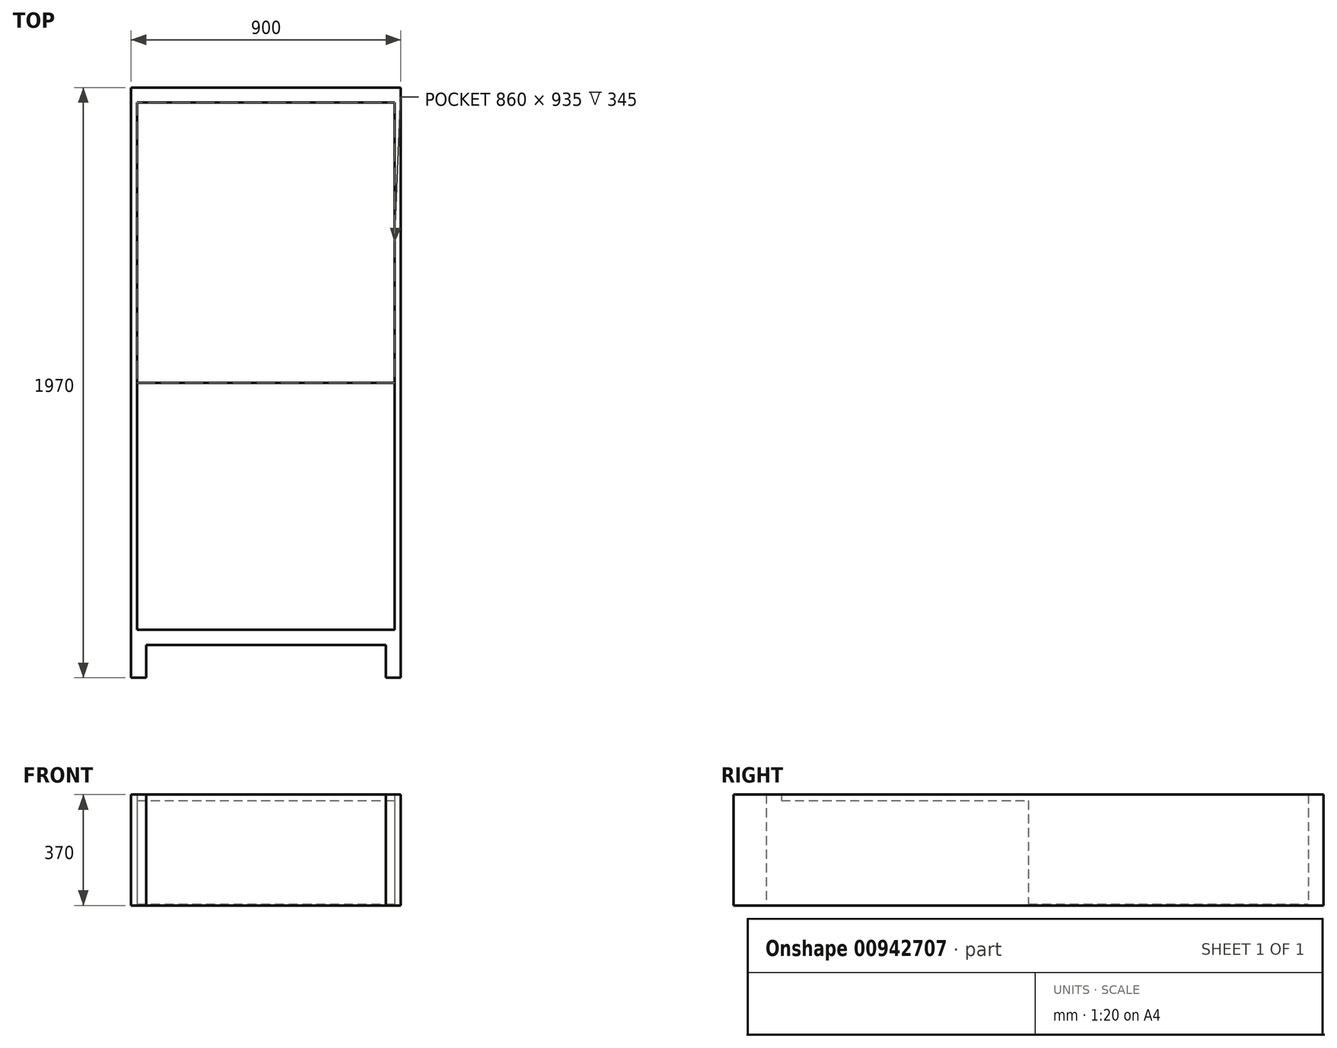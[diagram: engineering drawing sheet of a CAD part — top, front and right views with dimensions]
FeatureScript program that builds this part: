
annotation { "Feature Type Name" : "Feature", "Feature Type Description" : "" }
export const myFeature = defineFeature(function(context is Context, id is Id, definition is map)
    precondition{}
    {
        {
            var Q0;
            Q0=qCreatedBy(makeId("Top.planeOp"),FACE);
            var sketch = newSketch(context, id + "F0", { "sketchPlane" : qUnion([Q0])});
            skLineSegment(sketch, "E0.bottom", {"start": v(-450, 985) * mm, "end": v(450, 985) * mm});
            skLineSegment(sketch, "E0.left", {"start": v(-450, 985) * mm, "end": v(-450, -985) * mm});
            skLineSegment(sketch, "E0.right", {"start": v(450, 985) * mm, "end": v(450, -985) * mm});
            skLineSegment(sketch, "E1", {"start": v(-450, 0) * mm, "end": v(0, 0) * mm, "construction": true});
            skLineSegment(sketch, "E2", {"start": v(0, 0) * mm, "end": v(450, 0) * mm, "construction": true});
            skLineSegment(sketch, "E3", {"start": v(0, -985) * mm, "end": v(0, 0) * mm, "construction": true});
            skLineSegment(sketch, "E4", {"start": v(0, 0) * mm, "end": v(0, 985) * mm, "construction": true});
            skLineSegment(sketch, "E5", {"start": v(-400, -985) * mm, "end": v(-400, -875) * mm});
            skLineSegment(sketch, "E6", {"start": v(-400, -875) * mm, "end": v(400, -875) * mm});
            skLineSegment(sketch, "E7", {"start": v(400, -875) * mm, "end": v(400, -985) * mm});
            skLineSegment(sketch, "E8.trimOffspring", {"start": v(400, -985) * mm, "end": v(450, -985) * mm});
            skLineSegment(sketch, "E9", {"start": v(-400, -985) * mm, "end": v(-450, -985) * mm});
            skLineSegment(sketch, "E10.bottom", {"start": v(-430, -825) * mm, "end": v(430, -825) * mm});
            skLineSegment(sketch, "E10.top", {"start": v(-430, 935) * mm, "end": v(430, 935) * mm});
            skLineSegment(sketch, "E10.left", {"start": v(-430, -825) * mm, "end": v(-430, 935) * mm});
            skLineSegment(sketch, "E10.right", {"start": v(430, -825) * mm, "end": v(430, 935) * mm});
            skLineSegment(sketch, "E11", {"start": v(-430, 0) * mm, "end": v(430, 0) * mm});
            skSolve(sketch);
        }
        {
            var Q0;
            Q0=makeQuery(id+"F0.imprint","IMPRINT",FACE,{"disambiguationData":[TD([[makeQuery(id+"F0.imprint","IMPRINT",EDGE,{"derivedFrom":sQuery(id+"F0.wireOp",EDGE,"E0.bottom")}),-1.0]])]});
            extrude(context, id + "F1", {"entities" : qUnion([Q0]), "depth" : 370 * mm, "offsetDistance" : 25 * mm});
        }
        {
            var Q0;
            Q0=makeQuery(id+"F0.imprint","IMPRINT",FACE,{"disambiguationData":[TD([[makeQuery(id+"F0.imprint","IMPRINT",EDGE,{"derivedFrom":sQuery(id+"F0.wireOp",EDGE,"E10.bottom")}),1.0]])]});
            var Q1;
            {var subQ0=sQuery(id+"F0.wireOp",EDGE,"E10.top");Q1=makeQuery(id+"F0.imprint","IMPRINT",FACE,{"disambiguationData":[TD([[makeQuery(id+"F0.imprint","IMPRINT",EDGE,{"derivedFrom":subQ0}),-1.0]])]});}
            extrude(context, id + "F2", {"entities" : qUnion([Q0, Q1]), "operationType" : NewBodyOperationType.ADD, "depth" : 5 * mm, "offsetDistance" : 25 * mm});
        }
        {
            var Q0;
            Q0=makeQuery(id+"F1.opExtrude","SWEPT_BODY",BODY,{"disambiguationData":[OSD([sQuery(id+"F0.wireOp",EDGE,"E0.bottom"),sQuery(id+"F0.wireOp",EDGE,"E0.left"),sQuery(id+"F0.wireOp",EDGE,"E0.right"),sQuery(id+"F0.wireOp",EDGE,"E5"),sQuery(id+"F0.wireOp",EDGE,"E6"),sQuery(id+"F0.wireOp",EDGE,"E7"),sQuery(id+"F0.wireOp",EDGE,"E8.trimOffspring"),sQuery(id+"F0.wireOp",EDGE,"E9"),sQuery(id+"F0.wireOp",EDGE,"E10.bottom"),sQuery(id+"F0.wireOp",EDGE,"E10.top"),sQuery(id+"F0.wireOp",EDGE,"E10.left"),sQuery(id+"F0.wireOp",EDGE,"E10.right")])]});
            transform(context, id + "F3", {"entities" : qUnion([Q0]), "transformType" : TransformType.TRANSLATION_3D, "dx" : 0 * mm, "dy" : 0 * mm, "dz" : 0 * mm, "makeCopy" : true});
        }
        {
            var Q0;
            {var subQ0=sQuery(id+"F0.wireOp",EDGE,"E10.bottom");Q0=makeQuery(id+"F0.imprint","IMPRINT",FACE,{"disambiguationData":[TD([[makeQuery(id+"F0.imprint","IMPRINT",EDGE,{"derivedFrom":subQ0}),1.0]])]});}
            extrude(context, id + "F4", {"entities" : qUnion([Q0]), "operationType" : NewBodyOperationType.ADD, "depth" : 350 * mm, "offsetDistance" : 25 * mm});
        }
    });
